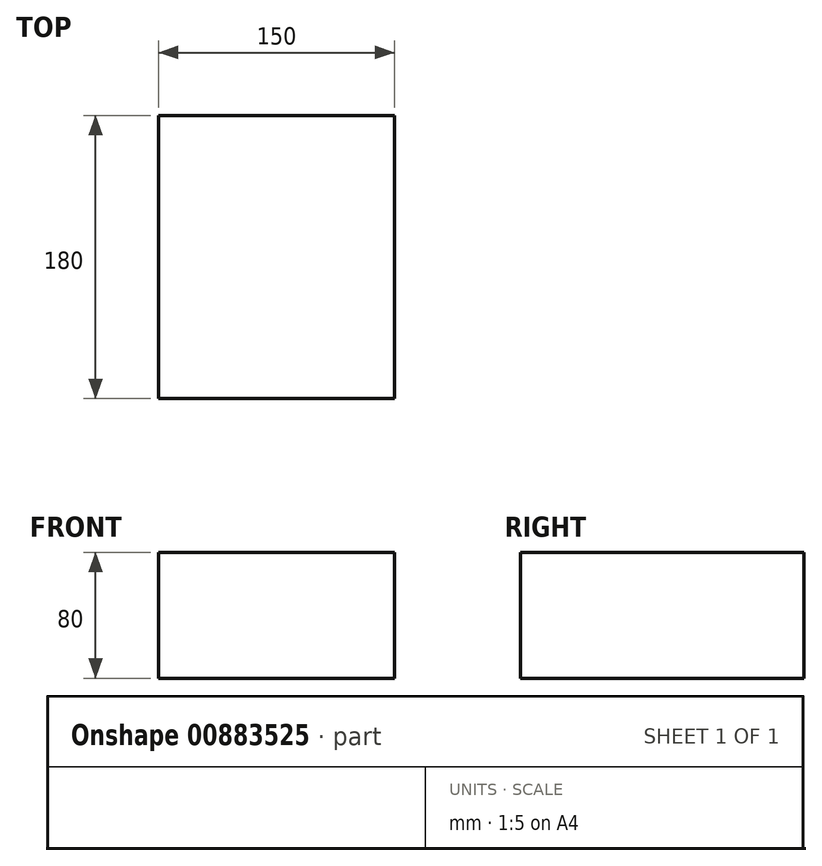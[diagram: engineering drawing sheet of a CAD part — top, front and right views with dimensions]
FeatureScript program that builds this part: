
annotation { "Feature Type Name" : "Feature", "Feature Type Description" : "" }
export const myFeature = defineFeature(function(context is Context, id is Id, definition is map)
    precondition{}
    {
        {
            var Q0;
            Q0=qCreatedBy(makeId("Top.planeOp"),FACE);
            var sketch = newSketch(context, id + "F0", { "sketchPlane" : qUnion([Q0])});
            skLineSegment(sketch, "E0.bottom", {"start": v(-75, 0) * mm, "end": v(75, 0) * mm});
            skLineSegment(sketch, "E0.top", {"start": v(-75, -180) * mm, "end": v(75, -180) * mm});
            skLineSegment(sketch, "E0.left", {"start": v(-75, 0) * mm, "end": v(-75, -180) * mm});
            skLineSegment(sketch, "E0.right", {"start": v(75, 0) * mm, "end": v(75, -180) * mm});
            skSolve(sketch);
        }
        {
            var Q0;
            Q0 = qSketchRegion(id + "F0", true);
            extrude(context, id + "F1", {"entities" : qUnion([Q0]), "oppositeDirection" : true, "depth" : 80 * mm, "offsetDistance" : 25.4 * mm});
        }
    });
